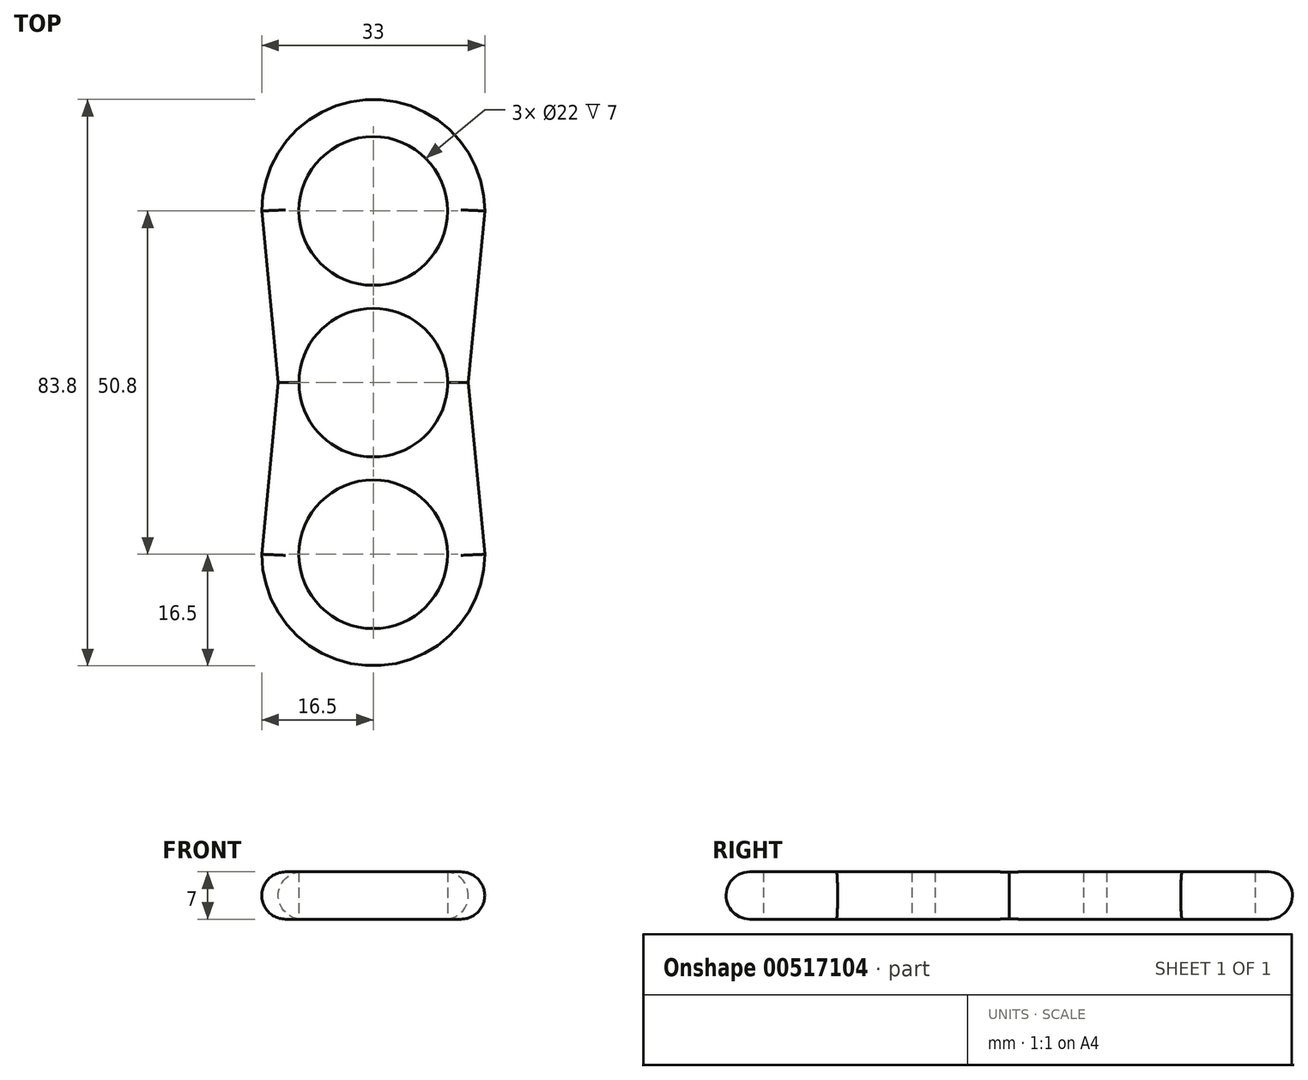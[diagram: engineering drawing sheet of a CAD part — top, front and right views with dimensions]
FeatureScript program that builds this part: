
annotation { "Feature Type Name" : "Feature", "Feature Type Description" : "" }
export const myFeature = defineFeature(function(context is Context, id is Id, definition is map)
    precondition{}
    {
        {
            var Q0;
            Q0=qCreatedBy(makeId("Top.planeOp"),FACE);
            var sketch = newSketch(context, id + "F0", { "sketchPlane" : qUnion([Q0])});
            skCircle(sketch, "E0", {"center": v(0, 0) * mm, "radius": 11 * mm});
            skCircle(sketch, "E1", {"center": v(0, 25.4) * mm, "radius": 11 * mm});
            skArc(sketch, "E2", {"start": v(16.2, 22.26) * mm, "mid": v(0, 41.9) * mm, "end": v(-16.2, 22.26) * mm});
            skCircle(sketch, "E3", {"center": v(0, -25.4) * mm, "radius": 11 * mm});
            skArc(sketch, "E4", {"start": v(-16.2, -22.26) * mm, "mid": v(0, -41.9) * mm, "end": v(16.2, -22.26) * mm});
            skLineSegment(sketch, "E5", {"start": v(16.5, 25.4) * mm, "end": v(14.06, 0) * mm});
            skLineSegment(sketch, "E6", {"start": v(16.5, -25.4) * mm, "end": v(14.06, 0) * mm});
            skLineSegment(sketch, "E7", {"start": v(-16.5, 25.4) * mm, "end": v(-14.06, 0) * mm});
            skLineSegment(sketch, "E8", {"start": v(-16.5, -25.4) * mm, "end": v(-14.06, 0) * mm});
            skSolve(sketch);
        }
        {
            var Q0;
            Q0=makeQuery(id+"F0.imprint","IMPRINT",FACE,{"disambiguationData":[TD([[makeQuery(id+"F0.imprint","IMPRINT",EDGE,{"derivedFrom":sQuery(id+"F0.wireOp",EDGE,"E0")}),-1.0]])]});
            extrude(context, id + "F1", {"entities" : qUnion([Q0]), "depth" : 7 * mm, "offsetDistance" : 25.4 * mm});
        }
        {
            var Q0;
            Q0=makeQuery(id+"F1.opExtrude","CAP_EDGE",EDGE,{"disambiguationData":[OSD([sQuery(id+"F0.wireOp",EDGE,"E5")])],"isStart":false});
            var Q1;
            Q1=makeQuery(id+"F1.opExtrude","CAP_EDGE",EDGE,{"disambiguationData":[OSD([sQuery(id+"F0.wireOp",EDGE,"E6")])],"isStart":false});
            var Q2;
            Q2=makeQuery(id+"F1.opExtrude","CAP_EDGE",EDGE,{"disambiguationData":[OSD([sQuery(id+"F0.wireOp",EDGE,"E4")])],"isStart":false});
            var Q3;
            Q3=makeQuery(id+"F1.opExtrude","CAP_EDGE",EDGE,{"disambiguationData":[OSD([sQuery(id+"F0.wireOp",EDGE,"E8")])],"isStart":false});
            var Q4;
            Q4=makeQuery(id+"F1.opExtrude","CAP_EDGE",EDGE,{"disambiguationData":[OSD([sQuery(id+"F0.wireOp",EDGE,"E7")])],"isStart":false});
            var Q5;
            Q5=makeQuery(id+"F1.opExtrude","CAP_EDGE",EDGE,{"disambiguationData":[OSD([sQuery(id+"F0.wireOp",EDGE,"E2")])],"isStart":false});
            var Q6;
            Q6=makeQuery(id+"F1.opExtrude","CAP_EDGE",EDGE,{"disambiguationData":[OSD([sQuery(id+"F0.wireOp",EDGE,"E7")])],"isStart":true});
            var Q7;
            Q7=makeQuery(id+"F1.opExtrude","CAP_EDGE",EDGE,{"disambiguationData":[OSD([sQuery(id+"F0.wireOp",EDGE,"E2")])],"isStart":true});
            var Q8;
            Q8=makeQuery(id+"F1.opExtrude","CAP_EDGE",EDGE,{"disambiguationData":[OSD([sQuery(id+"F0.wireOp",EDGE,"E5")])],"isStart":true});
            var Q9;
            Q9=makeQuery(id+"F1.opExtrude","CAP_EDGE",EDGE,{"disambiguationData":[OSD([sQuery(id+"F0.wireOp",EDGE,"E6")])],"isStart":true});
            var Q10;
            Q10=makeQuery(id+"F1.opExtrude","CAP_EDGE",EDGE,{"disambiguationData":[OSD([sQuery(id+"F0.wireOp",EDGE,"E4")])],"isStart":true});
            var Q11;
            Q11=makeQuery(id+"F1.opExtrude","CAP_EDGE",EDGE,{"disambiguationData":[OSD([sQuery(id+"F0.wireOp",EDGE,"E8")])],"isStart":true});
            fillet(context, id + "F2", {"entities" : qUnion([Q0, Q1, Q2, Q3, Q4, Q5, Q6, Q7, Q8, Q9, Q10, Q11]), "radius" : 3.5 * mm, "tangentPropagation" : true, "allowEdgeOverflow" : false});
        }
    });
